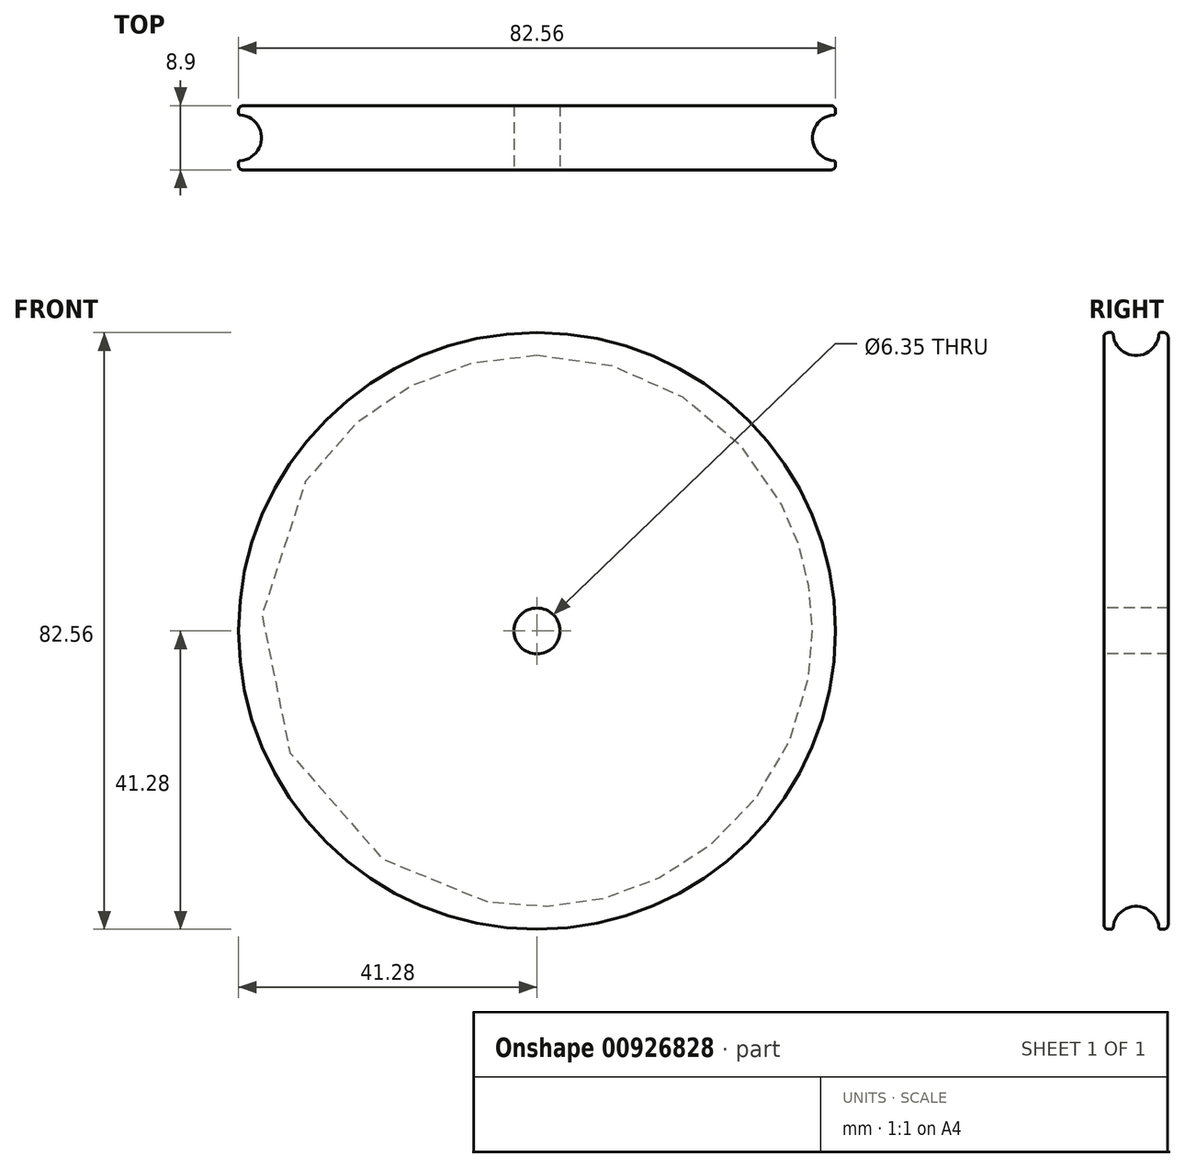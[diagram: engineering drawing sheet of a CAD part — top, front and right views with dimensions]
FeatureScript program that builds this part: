
annotation { "Feature Type Name" : "Feature", "Feature Type Description" : "" }
export const myFeature = defineFeature(function(context is Context, id is Id, definition is map)
    precondition{}
    {
        {
            var Q0;
            Q0=qCreatedBy(makeId("Top.planeOp"),FACE);
            var sketch = newSketch(context, id + "F0", { "sketchPlane" : qUnion([Q0])});
            skLineSegment(sketch, "E0.bottom", {"start": v(0, 4.45) * mm, "end": v(41.28, 4.45) * mm});
            skLineSegment(sketch, "E0.top", {"start": v(0, -4.45) * mm, "end": v(41.28, -4.45) * mm});
            skLineSegment(sketch, "E0.left", {"start": v(0, 4.45) * mm, "end": v(0, -4.45) * mm});
            skLineSegment(sketch, "E0.right", {"start": v(41.28, 4.45) * mm, "end": v(41.28, -4.45) * mm});
            skCircle(sketch, "E1", {"center": v(41.28, 0) * mm, "radius": 3.18 * mm});
            skSolve(sketch);
        }
        {
            var Q0;
            {var subQ1=sQuery(id+"F0.wireOp",EDGE,"E0.bottom");Q0=makeQuery(id+"F0.imprint","IMPRINT",FACE,{"disambiguationData":[TD([[makeQuery(id+"F0.imprint","IMPRINT",EDGE,{"derivedFrom":subQ1}),-1.0]])]});}
            var Q1;
            Q1=sQuery(id+"F0.wireOp",EDGE,"E0.left");
            revolve(context, id + "F1", {"surfaceOperationType" : NewSurfaceOperationType.NEW, "entities" : qUnion([Q0]), "axis" : qUnion([Q1]), "revolveType" : RevolveType.FULL});
        }
        {
            var Q0;
            Q0=makeQuery(id+"F1.opRevolve","SWEPT_EDGE",EDGE,{"disambiguationData":[OSD([sQuery(id+"F0.wireOp",EDGE,"E0.bottom"),sQuery(id+"F0.wireOp",EDGE,"E0.right")])]});
            var Q1;
            Q1=makeQuery(id+"F1.opRevolve","SWEPT_EDGE",EDGE,{"disambiguationData":[OSD([sQuery(id+"F0.wireOp",EDGE,"E0.top"),sQuery(id+"F0.wireOp",EDGE,"E0.right")])]});
            fillet(context, id + "F2", {"entities" : qUnion([Q0, Q1]), "radius" : 0.64 * mm, "tangentPropagation" : true, "allowEdgeOverflow" : false});
        }
        {
            var Q0;
            {var subQ0=sQuery(id+"F0.wireOp",EDGE,"E1");var subQ1=sQuery(id+"F0.wireOp",EDGE,"E0.right");Q0=makeQuery(id+"F1.opRevolve","SWEPT_EDGE",EDGE,{"disambiguationData":[OSD([subQ1,subQ0]),TDD([makeQuery(id+"F0.imprint","INTERSECT",VERTEX,{"disambiguationData":[OD(0.0)],"derivedFrom":[subQ1,subQ0]})])]});}
            var Q1;
            {var subQ0=sQuery(id+"F0.wireOp",EDGE,"E1");var subQ1=sQuery(id+"F0.wireOp",EDGE,"E0.right");Q1=makeQuery(id+"F1.opRevolve","SWEPT_EDGE",EDGE,{"disambiguationData":[OSD([subQ1,subQ0]),TDD([makeQuery(id+"F0.imprint","INTERSECT",VERTEX,{"disambiguationData":[OD(1.0)],"derivedFrom":[subQ1,subQ0]})])]});}
            fillet(context, id + "F3", {"entities" : qUnion([Q0, Q1]), "radius" : 0.25 * mm, "tangentPropagation" : true, "allowEdgeOverflow" : false});
        }
        {
            var Q0;
            Q0=makeQuery(id+"F1.opRevolve","SWEPT_FACE",FACE,{"disambiguationData":[OSD([sQuery(id+"F0.wireOp",EDGE,"E0.top")])]});
            var sketch = newSketch(context, id + "F4", { "sketchPlane" : qUnion([Q0])});
            skCircle(sketch, "E2", {"center": v(0, 0) * mm, "radius": 3.18 * mm});
            skSolve(sketch);
        }
        {
            var Q0;
            Q0=makeQuery(id+"F4.imprint","IMPRINT",FACE,{"disambiguationData":[TD([[makeQuery(id+"F4.imprint","IMPRINT",EDGE,{"derivedFrom":sQuery(id+"F4.wireOp",EDGE,"E2")}),1.0]])]});
            extrude(context, id + "F5", {"entities" : qUnion([Q0]), "operationType" : NewBodyOperationType.REMOVE, "endBound" : BoundingType.THROUGH_ALL, "oppositeDirection" : true, "depth" : 25.4 * mm, "offsetDistance" : 25.4 * mm});
        }
    });
